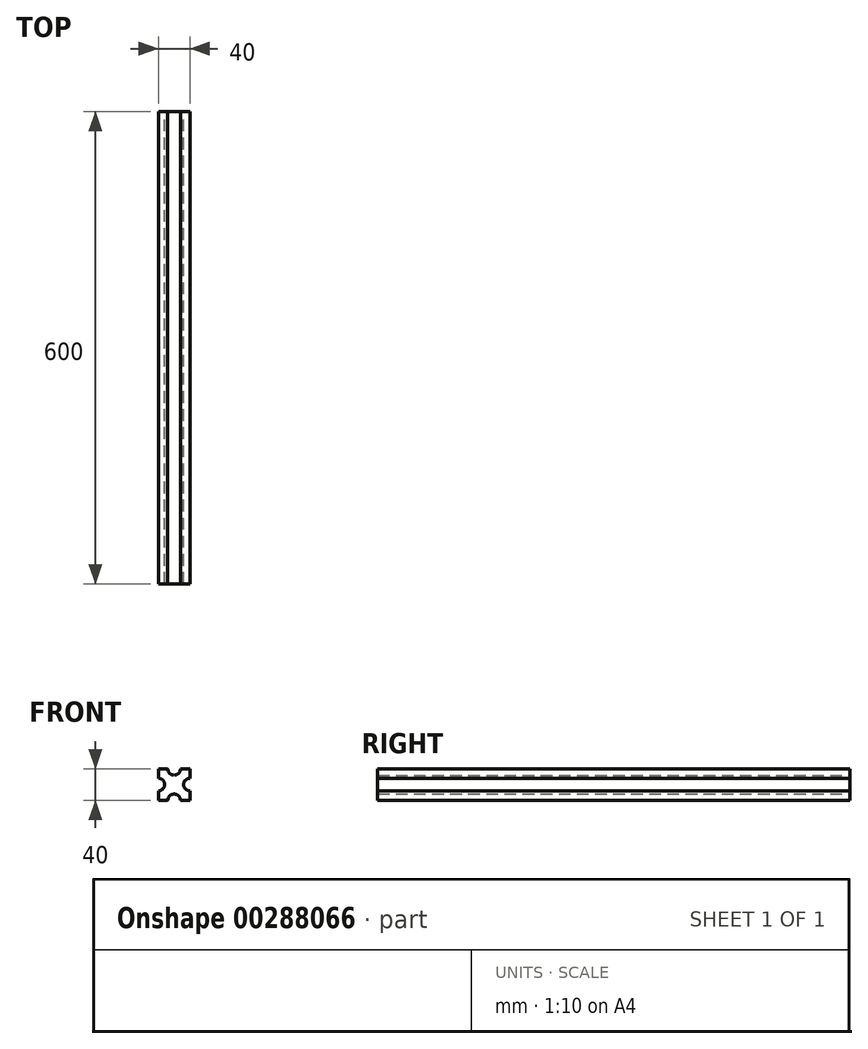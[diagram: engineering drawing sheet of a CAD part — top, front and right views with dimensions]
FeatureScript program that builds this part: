
annotation { "Feature Type Name" : "Feature", "Feature Type Description" : "" }
export const myFeature = defineFeature(function(context is Context, id is Id, definition is map)
    precondition{}
    {
        {
            var Q0;
            Q0=qCreatedBy(makeId("Front.planeOp"),FACE);
            var sketch = newSketch(context, id + "F0", { "sketchPlane" : qUnion([Q0])});
            skLineSegment(sketch, "E0.bottom", {"start": v(20, -20) * mm, "end": v(-20, -20) * mm});
            skLineSegment(sketch, "E0.top", {"start": v(20, 20) * mm, "end": v(-20, 20) * mm});
            skLineSegment(sketch, "E0.left", {"start": v(20, -20) * mm, "end": v(20, 20) * mm});
            skLineSegment(sketch, "E0.right", {"start": v(-20, -20) * mm, "end": v(-20, 20) * mm});
            skPoint(sketch, "E0.middle", {"position": v(0, 0) * mm});
            skCircle(sketch, "E1", {"center": v(0, 20) * mm, "radius": 8 * mm});
            skCircle(sketch, "E2", {"center": v(-20, 0) * mm, "radius": 8 * mm});
            skCircle(sketch, "E3", {"center": v(0, -20) * mm, "radius": 8 * mm});
            skCircle(sketch, "E4", {"center": v(20, 0) * mm, "radius": 8 * mm});
            skSolve(sketch);
        }
        {
            var Q0;
            {var subQ4=sQuery(id+"F0.wireOp",EDGE,"E0.bottom");var subQ6=sQuery(id+"F0.wireOp",EDGE,"E0.left");var subQ11=makeQuery(id+"F0.imprint","INTERSECT",VERTEX,{"derivedFrom":[subQ4,subQ6]});Q0=makeQuery(id+"F0.imprint","IMPRINT",FACE,{"disambiguationData":[TD([[makeQuery(id+"F0.imprint","IMPRINT",EDGE,{"disambiguationData":[TD([[subQ11,-1.0]])],"derivedFrom":subQ4}),-1.0]])]});}
            extrude(context, id + "F1", {"entities" : qUnion([Q0]), "depth" : 600 * mm});
        }
    });
